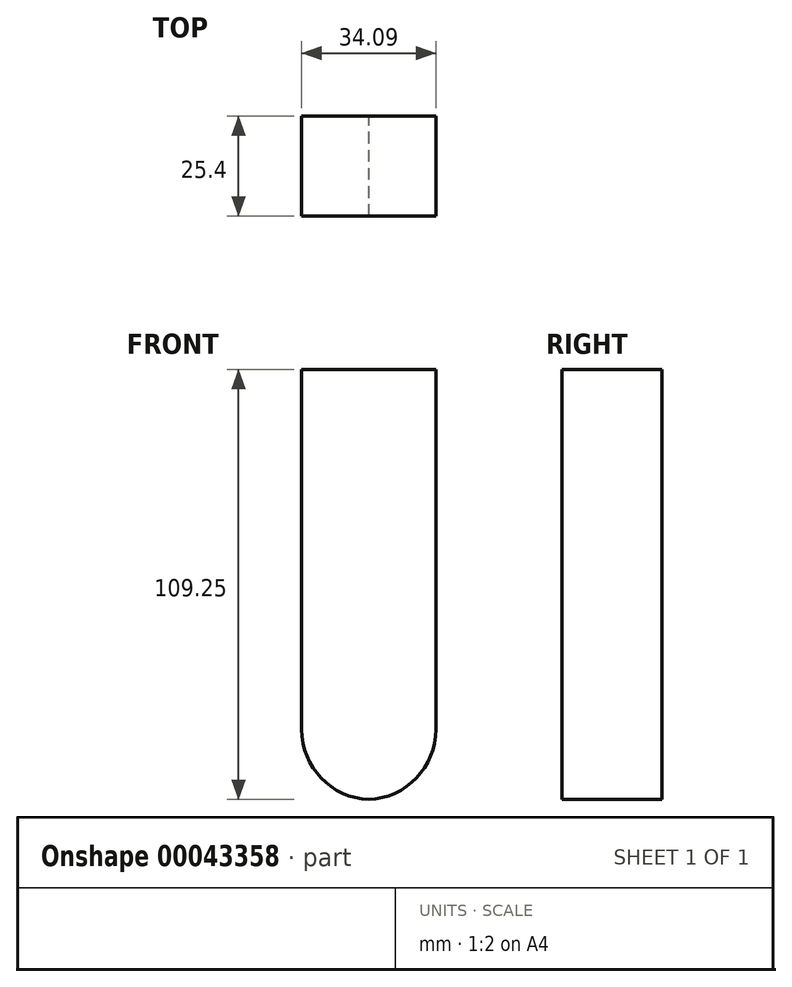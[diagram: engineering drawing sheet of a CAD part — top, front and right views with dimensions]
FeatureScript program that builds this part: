
annotation { "Feature Type Name" : "Feature", "Feature Type Description" : "" }
export const myFeature = defineFeature(function(context is Context, id is Id, definition is map)
    precondition{}
    {
        {
            var Q0;
            Q0=qCreatedBy(makeId("Front.planeOp"),FACE);
            var sketch = newSketch(context, id + "F0", { "sketchPlane" : qUnion([Q0])});
            skLineSegment(sketch, "E0.bottom", {"start": v(-30.8, 41.85) * mm, "end": v(3.3, 41.85) * mm});
            skLineSegment(sketch, "E0.top", {"start": v(-30.8, -67.42) * mm, "end": v(3.3, -67.42) * mm});
            skLineSegment(sketch, "E0.left", {"start": v(-30.8, 41.85) * mm, "end": v(-30.8, -67.42) * mm});
            skLineSegment(sketch, "E0.right", {"start": v(3.3, 41.85) * mm, "end": v(3.3, -67.42) * mm});
            skSolve(sketch);
        }
        {
            var Q0;
            Q0 = qSketchRegion(id + "F0", true);
            extrude(context, id + "F1", {"entities" : qUnion([Q0]), "depth" : 25.4 * mm});
        }
        {
            var Q0;
            Q0=makeQuery(id+"F1.opExtrude","SWEPT_EDGE",EDGE,{"disambiguationData":[OSD([sQuery(id+"F0.wireOp",EDGE,"E0.top"),sQuery(id+"F0.wireOp",EDGE,"E0.left")])]});
            var Q1;
            Q1=makeQuery(id+"F1.opExtrude","SWEPT_EDGE",EDGE,{"disambiguationData":[OSD([sQuery(id+"F0.wireOp",EDGE,"E0.top"),sQuery(id+"F0.wireOp",EDGE,"E0.right")])]});
            fillet(context, id + "F2", {"entities" : qUnion([Q0, Q1]), "radius" : 17.78 * mm, "tangentPropagation" : true, "allowEdgeOverflow" : false});
        }
    });
